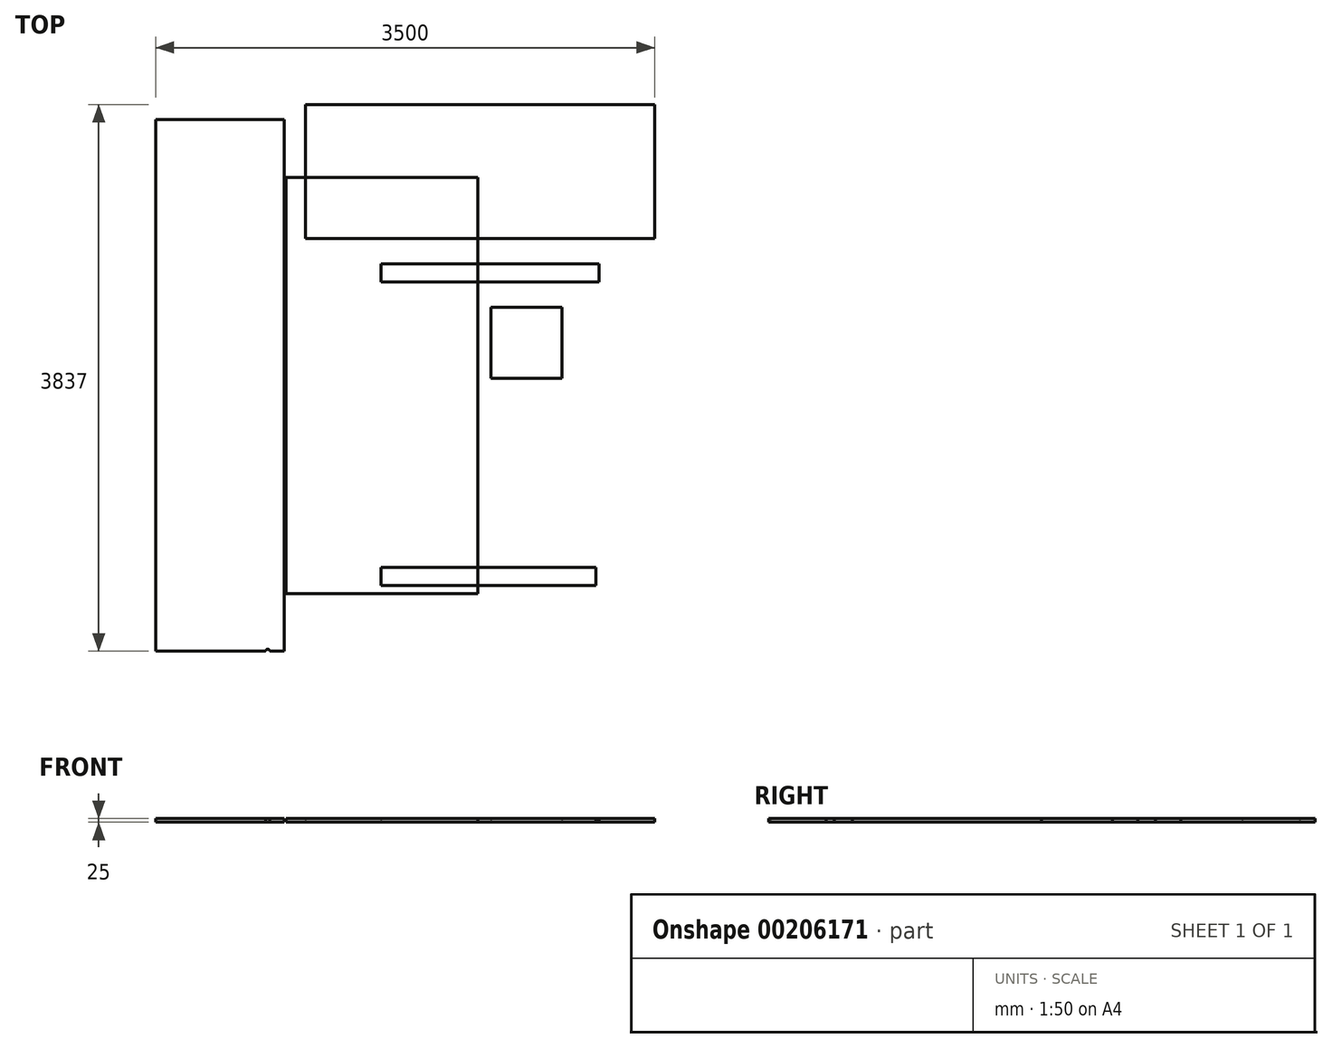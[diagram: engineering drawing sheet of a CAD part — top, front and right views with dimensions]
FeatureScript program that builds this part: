
annotation { "Feature Type Name" : "Feature", "Feature Type Description" : "" }
export const myFeature = defineFeature(function(context is Context, id is Id, definition is map)
    precondition{}
    {
        {
            var Q0;
            Q0=qCreatedBy(makeId("Top.planeOp"),FACE);
            var sketch = newSketch(context, id + "F0", { "sketchPlane" : qUnion([Q0])});
            skLineSegment(sketch, "E0.bottom", {"start": v(-18060.05, -1536.7) * mm, "end": v(-19088.75, -1536.7) * mm});
            skLineSegment(sketch, "E0.top", {"start": v(-18060.05, 1536.7) * mm, "end": v(-19088.75, 1536.7) * mm});
            skLineSegment(sketch, "E0.left", {"start": v(-18060.05, -1536.7) * mm, "end": v(-18060.05, 1536.7) * mm});
            skLineSegment(sketch, "E0.right", {"start": v(-19088.75, -1536.7) * mm, "end": v(-19088.75, 1536.7) * mm});
            skPoint(sketch, "E0.middle", {"position": v(-18574.4, 0) * mm});
            skLineSegment(sketch, "E1.bottom", {"start": v(1809.1, -1460.5) * mm, "end": v(462.9, -1460.5) * mm});
            skLineSegment(sketch, "E1.top", {"start": v(1809.1, 1460.5) * mm, "end": v(462.9, 1460.5) * mm});
            skLineSegment(sketch, "E1.left", {"start": v(1809.1, -1460.5) * mm, "end": v(1809.1, 1460.5) * mm});
            skLineSegment(sketch, "E1.right", {"start": v(462.9, -1460.5) * mm, "end": v(462.9, 1460.5) * mm});
            skPoint(sketch, "E1.middle", {"position": v(1136, 0) * mm});
            skLineSegment(sketch, "E2", {"start": v(-18574.4, 0) * mm, "end": v(1136, 0) * mm});
            skCircle(sketch, "E3", {"center": v(-20707.4, 0) * mm, "radius": 150 * mm});
            skLineSegment(sketch, "E4.bottom", {"start": v(2402, 50) * mm, "end": v(1902, 50) * mm});
            skLineSegment(sketch, "E4.top", {"start": v(2402, 550) * mm, "end": v(1902, 550) * mm});
            skLineSegment(sketch, "E4.left", {"start": v(2402, 50) * mm, "end": v(2402, 550) * mm});
            skLineSegment(sketch, "E4.right", {"start": v(1902, 50) * mm, "end": v(1902, 550) * mm});
            skPoint(sketch, "E4.middle", {"position": v(2152, 300) * mm});
            skSolve(sketch);
        }
        {
            var Q0;
            Q0=qCreatedBy(makeId("Top.planeOp"),FACE);
            var sketch = newSketch(context, id + "F1", { "sketchPlane" : qUnion([Q0])});
            skLineSegment(sketch, "E5.bottom", {"start": v(450, -1865) * mm, "end": v(-450, -1865) * mm});
            skLineSegment(sketch, "E5.top", {"start": v(450, 1865) * mm, "end": v(-450, 1865) * mm});
            skLineSegment(sketch, "E5.left", {"start": v(450, -1865) * mm, "end": v(450, 1865) * mm});
            skLineSegment(sketch, "E5.right", {"start": v(-450, -1865) * mm, "end": v(-450, 1865) * mm});
            skPoint(sketch, "E5.middle", {"position": v(0, 0) * mm});
            skLineSegment(sketch, "E6.bottom", {"start": v(600, 1030) * mm, "end": v(3050, 1030) * mm});
            skLineSegment(sketch, "E6.top", {"start": v(600, 1972) * mm, "end": v(3050, 1972) * mm});
            skLineSegment(sketch, "E6.left", {"start": v(600, 1030) * mm, "end": v(600, 1972) * mm});
            skLineSegment(sketch, "E6.right", {"start": v(3050, 1030) * mm, "end": v(3050, 1972) * mm});
            skPoint(sketch, "E6.middle", {"position": v(1825, 1501) * mm});
            skLineSegment(sketch, "E7.bottom", {"start": v(2402, 50) * mm, "end": v(1902, 50) * mm});
            skLineSegment(sketch, "E7.top", {"start": v(2402, 550) * mm, "end": v(1902, 550) * mm});
            skLineSegment(sketch, "E7.left", {"start": v(2402, 50) * mm, "end": v(2402, 550) * mm});
            skLineSegment(sketch, "E7.right", {"start": v(1902, 50) * mm, "end": v(1902, 550) * mm});
            skPoint(sketch, "E7.middle", {"position": v(2152, 300) * mm});
            skLineSegment(sketch, "E8.bottom", {"start": v(2637, -1402.5) * mm, "end": v(1132, -1402.5) * mm});
            skLineSegment(sketch, "E8.top", {"start": v(2637, -1277.5) * mm, "end": v(1132, -1277.5) * mm});
            skLineSegment(sketch, "E8.left", {"start": v(2637, -1402.5) * mm, "end": v(2637, -1277.5) * mm});
            skLineSegment(sketch, "E8.right", {"start": v(1132, -1402.5) * mm, "end": v(1132, -1277.5) * mm});
            skPoint(sketch, "E8.middle", {"position": v(1884.5, -1340) * mm});
            skLineSegment(sketch, "E9.bottom", {"start": v(2661.94, 727.5) * mm, "end": v(1132, 727.5) * mm});
            skLineSegment(sketch, "E9.top", {"start": v(2661.94, 852.5) * mm, "end": v(1132, 852.5) * mm});
            skLineSegment(sketch, "E9.left", {"start": v(2661.94, 727.5) * mm, "end": v(2661.94, 852.5) * mm});
            skLineSegment(sketch, "E9.right", {"start": v(1132, 727.5) * mm, "end": v(1132, 852.5) * mm});
            skPoint(sketch, "E9.middle", {"position": v(1896.97, 790) * mm});
            skLineSegment(sketch, "E10.bottom", {"start": v(-18920, -1865) * mm, "end": v(-19990, -1865) * mm});
            skLineSegment(sketch, "E10.top", {"start": v(-18920, 1865) * mm, "end": v(-19990, 1865) * mm});
            skLineSegment(sketch, "E10.left", {"start": v(-18920, -1865) * mm, "end": v(-18920, 1865) * mm});
            skLineSegment(sketch, "E10.right", {"start": v(-19990, -1865) * mm, "end": v(-19990, 1865) * mm});
            skPoint(sketch, "E10.middle", {"position": v(-19455, 0) * mm});
            skLineSegment(sketch, "E11.bottom", {"start": v(-20645, 330) * mm, "end": v(-21165, 330) * mm});
            skLineSegment(sketch, "E11.top", {"start": v(-20645, 670) * mm, "end": v(-21165, 670) * mm});
            skLineSegment(sketch, "E11.left", {"start": v(-20645, 330) * mm, "end": v(-20645, 670) * mm});
            skLineSegment(sketch, "E11.right", {"start": v(-21165, 330) * mm, "end": v(-21165, 670) * mm});
            skPoint(sketch, "E11.middle", {"position": v(-20905, 500) * mm});
            skLineSegment(sketch, "E12.bottom", {"start": v(-20645, -670) * mm, "end": v(-21165, -670) * mm});
            skLineSegment(sketch, "E12.top", {"start": v(-20645, -330) * mm, "end": v(-21165, -330) * mm});
            skLineSegment(sketch, "E12.left", {"start": v(-20645, -670) * mm, "end": v(-20645, -330) * mm});
            skLineSegment(sketch, "E12.right", {"start": v(-21165, -670) * mm, "end": v(-21165, -330) * mm});
            skPoint(sketch, "E12.middle", {"position": v(-20905, -500) * mm});
            skPoint(sketch, "E13", {"position": v(-20905, -330) * mm});
            skLineSegment(sketch, "E14", {"start": v(0, 0) * mm, "end": v(-19455, 0) * mm});
            skCircle(sketch, "E15", {"center": v(1202, -1340) * mm, "radius": 15 * mm});
            skCircle(sketch, "E16", {"center": v(335, -1866.07) * mm, "radius": 15 * mm});
            skCircle(sketch, "E17", {"center": v(1202, 790) * mm, "radius": 15 * mm});
            skSolve(sketch);
        }
        {
            var Q0;
            {var subQ1=sQuery(id+"F0.wireOp",EDGE,"E1.bottom");Q0=makeQuery(id+"F0.imprint","IMPRINT",FACE,{"disambiguationData":[TD([[makeQuery(id+"F0.imprint","IMPRINT",EDGE,{"derivedFrom":subQ1}),-1.0]])]});}
            var Q1;
            Q1=makeQuery(id+"F1.imprint","IMPRINT",FACE,{"disambiguationData":[TD([[makeQuery(id+"F1.imprint","IMPRINT",EDGE,{"derivedFrom":sQuery(id+"F1.wireOp",EDGE,"E6.bottom")}),1.0]])]});
            var Q2;
            {var subQ5=sQuery(id+"F1.wireOp",EDGE,"E5.top");Q2=makeQuery(id+"F1.imprint","IMPRINT",FACE,{"disambiguationData":[TD([[makeQuery(id+"F1.imprint","IMPRINT",EDGE,{"derivedFrom":subQ5}),1.0]])]});}
            var Q3;
            Q3=makeQuery(id+"F1.imprint","IMPRINT",FACE,{"disambiguationData":[TD([[makeQuery(id+"F1.imprint","IMPRINT",EDGE,{"derivedFrom":sQuery(id+"F1.wireOp",EDGE,"E8.bottom")}),-1.0]])]});
            var Q4;
            Q4=makeQuery(id+"F1.imprint","IMPRINT",FACE,{"disambiguationData":[TD([[makeQuery(id+"F1.imprint","IMPRINT",EDGE,{"derivedFrom":sQuery(id+"F1.wireOp",EDGE,"E9.bottom")}),-1.0]])]});
            var Q5;
            Q5=makeQuery(id+"F0.imprint","IMPRINT",FACE,{"disambiguationData":[TD([[makeQuery(id+"F0.imprint","IMPRINT",EDGE,{"derivedFrom":sQuery(id+"F0.wireOp",EDGE,"E4.bottom")}),-1.0]])]});
            var Q6;
            Q6=makeQuery(id+"F1.imprint","IMPRINT",FACE,{"disambiguationData":[TD([[makeQuery(id+"F1.imprint","IMPRINT",EDGE,{"derivedFrom":sQuery(id+"F1.wireOp",EDGE,"E7.bottom")}),-1.0]])]});
            var Q7;
            {var subQ0=sQuery(id+"F1.wireOp",EDGE,"E16");var subQ1=sQuery(id+"F1.wireOp",EDGE,"E5.bottom");var subQ2=makeQuery(id+"F1.imprint","INTERSECT",VERTEX,{"disambiguationData":[OD(0.0)],"derivedFrom":[subQ1,subQ0]});Q7=makeQuery(id+"F1.imprint","IMPRINT",FACE,{"disambiguationData":[TD([[makeQuery(id+"F1.imprint","IMPRINT",EDGE,{"disambiguationData":[TD([[subQ2,-1.0]])],"derivedFrom":subQ1}),1.0]])]});}
            var Q8;
            Q8=makeQuery(id+"F1.imprint","IMPRINT",FACE,{"disambiguationData":[TD([[makeQuery(id+"F1.imprint","IMPRINT",EDGE,{"derivedFrom":sQuery(id+"F1.wireOp",EDGE,"E17")}),1.0]])]});
            var Q9;
            {var subQ0=sQuery(id+"F1.wireOp",EDGE,"E16");var subQ1=sQuery(id+"F1.wireOp",EDGE,"E5.bottom");var subQ2=makeQuery(id+"F1.imprint","INTERSECT",VERTEX,{"disambiguationData":[OD(0.0)],"derivedFrom":[subQ1,subQ0]});Q9=makeQuery(id+"F1.imprint","IMPRINT",FACE,{"disambiguationData":[TD([[makeQuery(id+"F1.imprint","IMPRINT",EDGE,{"disambiguationData":[TD([[subQ2,-1.0]])],"derivedFrom":subQ1}),-1.0]])]});}
            var Q10;
            Q10=makeQuery(id+"F1.imprint","IMPRINT",FACE,{"disambiguationData":[TD([[makeQuery(id+"F1.imprint","IMPRINT",EDGE,{"derivedFrom":sQuery(id+"F1.wireOp",EDGE,"E15")}),1.0]])]});
            extrude(context, id + "F2", {"entities" : qUnion([Q0, Q1, Q2, Q3, Q4, Q5, Q6, Q7, Q8, Q9, Q10]), "depth" : 25 * mm});
        }
    });
